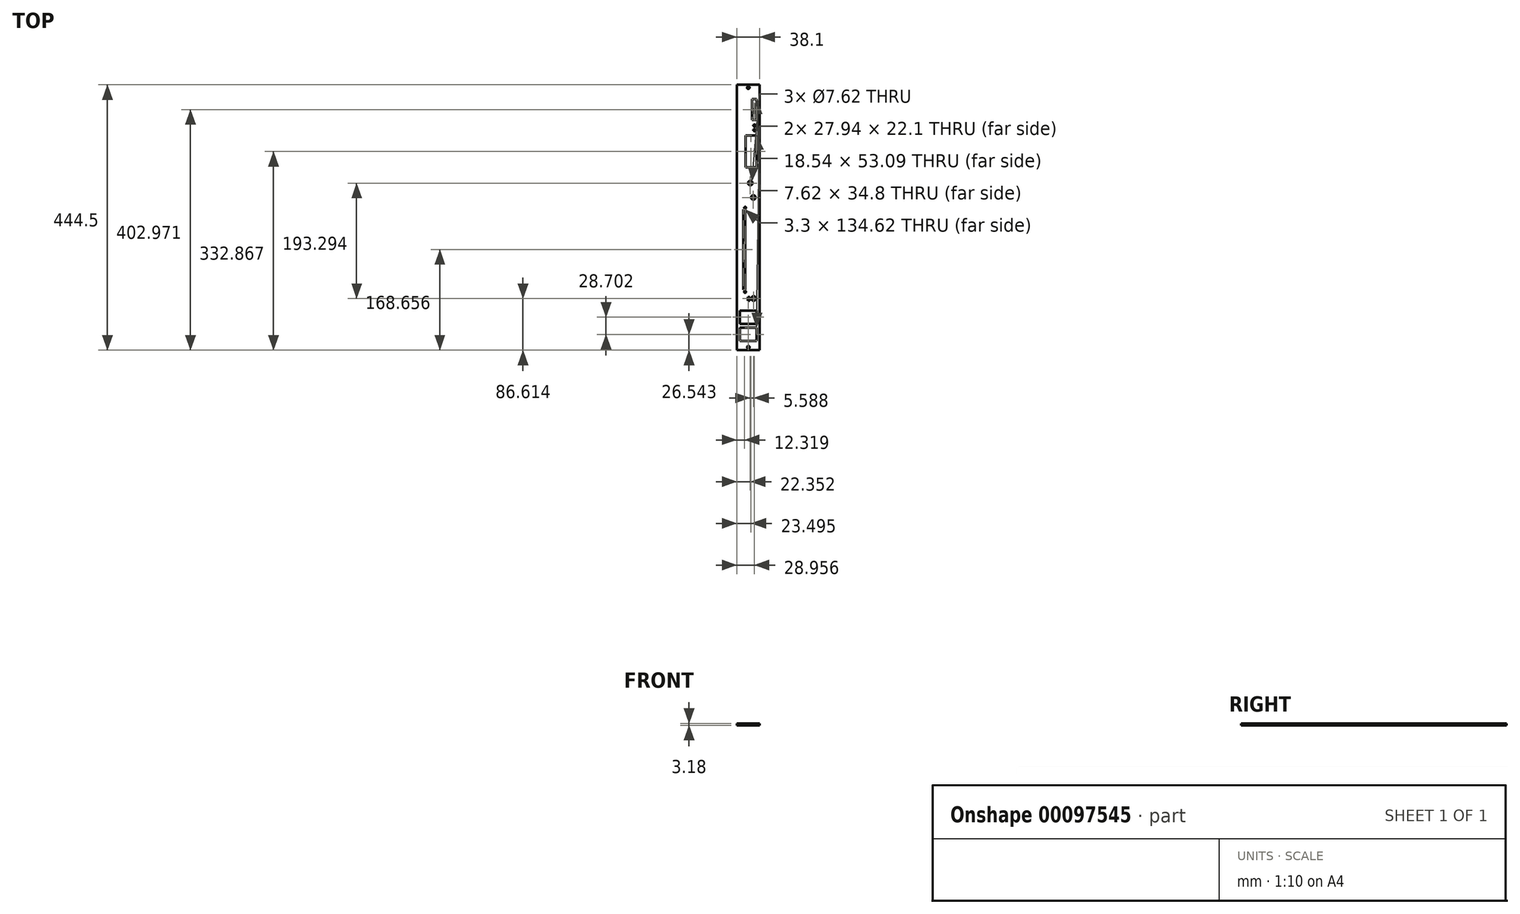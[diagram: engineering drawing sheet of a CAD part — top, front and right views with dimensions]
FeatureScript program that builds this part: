
annotation { "Feature Type Name" : "Feature", "Feature Type Description" : "" }
export const myFeature = defineFeature(function(context is Context, id is Id, definition is map)
    precondition{}
    {
        {
            var Q0;
            Q0=qCreatedBy(makeId("Top.planeOp"),FACE);
            var sketch = newSketch(context, id + "F0", { "sketchPlane" : qUnion([Q0])});
            skLineSegment(sketch, "E0.bottom", {"start": v(-19.05, 222.25) * mm, "end": v(19.05, 222.25) * mm});
            skLineSegment(sketch, "E0.top", {"start": v(-19.05, -222.25) * mm, "end": v(19.05, -222.25) * mm});
            skLineSegment(sketch, "E0.left", {"start": v(-19.05, 222.25) * mm, "end": v(-19.05, -222.25) * mm});
            skLineSegment(sketch, "E0.right", {"start": v(19.05, 222.25) * mm, "end": v(19.05, -222.25) * mm});
            skCircle(sketch, "E1", {"center": v(0, 217.55) * mm, "radius": 2.16 * mm});
            skLineSegment(sketch, "E2", {"start": v(0, 222.25) * mm, "end": v(0, -222.25) * mm, "construction": true});
            skCircle(sketch, "E3", {"center": v(0, -217.3) * mm, "radius": 2.16 * mm});
            skLineSegment(sketch, "E4.bottom", {"start": v(-13.97, -184.66) * mm, "end": v(13.97, -184.66) * mm});
            skLineSegment(sketch, "E4.top", {"start": v(-13.97, -206.76) * mm, "end": v(13.97, -206.76) * mm});
            skLineSegment(sketch, "E4.left", {"start": v(-13.97, -184.66) * mm, "end": v(-13.97, -206.76) * mm});
            skLineSegment(sketch, "E4.right", {"start": v(13.97, -184.66) * mm, "end": v(13.97, -206.76) * mm});
            skLineSegment(sketch, "E5.bottom", {"start": v(-13.97, -155.96) * mm, "end": v(13.97, -155.96) * mm});
            skLineSegment(sketch, "E5.top", {"start": v(-13.97, -178.05) * mm, "end": v(13.97, -178.05) * mm});
            skLineSegment(sketch, "E5.left", {"start": v(-13.97, -155.96) * mm, "end": v(-13.97, -178.05) * mm});
            skLineSegment(sketch, "E5.right", {"start": v(13.97, -155.96) * mm, "end": v(13.97, -178.05) * mm});
            skLineSegment(sketch, "E6.bottom", {"start": v(-8.38, 13.72) * mm, "end": v(-5.08, 13.72) * mm});
            skLineSegment(sketch, "E6.top", {"start": v(-8.38, -120.9) * mm, "end": v(-5.08, -120.9) * mm});
            skLineSegment(sketch, "E6.left", {"start": v(-8.38, 13.72) * mm, "end": v(-8.38, -120.9) * mm});
            skLineSegment(sketch, "E6.right", {"start": v(-5.08, 13.72) * mm, "end": v(-5.08, -120.9) * mm});
            skCircle(sketch, "E7", {"center": v(-5.33, -124.71) * mm, "radius": 1.52 * mm});
            skPoint(sketch, "E7.centerSnap0", {"position": v(-6.73, -120.9) * mm});
            skCircle(sketch, "E8", {"center": v(-5.33, 16.26) * mm, "radius": 1.52 * mm});
            skPoint(sketch, "E8.centerSnap0", {"position": v(-6.73, 13.72) * mm});
            skCircle(sketch, "E9", {"center": v(8.38, 33.53) * mm, "radius": 3.81 * mm});
            skCircle(sketch, "E10", {"center": v(3.3, 57.66) * mm, "radius": 3.81 * mm});
            skLineSegment(sketch, "E11.bottom", {"start": v(-4.83, 84.07) * mm, "end": v(13.72, 84.07) * mm});
            skLineSegment(sketch, "E11.top", {"start": v(-4.83, 137.16) * mm, "end": v(13.72, 137.16) * mm});
            skLineSegment(sketch, "E11.left", {"start": v(-4.83, 84.07) * mm, "end": v(-4.83, 137.16) * mm});
            skLineSegment(sketch, "E11.right", {"start": v(13.72, 84.07) * mm, "end": v(13.72, 137.16) * mm});
            skLineSegment(sketch, "E12.bottom", {"start": v(6.1, 198.12) * mm, "end": v(13.72, 198.12) * mm});
            skLineSegment(sketch, "E12.top", {"start": v(6.1, 163.32) * mm, "end": v(13.72, 163.32) * mm});
            skLineSegment(sketch, "E12.left", {"start": v(6.1, 198.12) * mm, "end": v(6.1, 163.32) * mm});
            skLineSegment(sketch, "E12.right", {"start": v(13.72, 198.12) * mm, "end": v(13.72, 163.32) * mm});
            skCircle(sketch, "E13", {"center": v(10.29, 154.05) * mm, "radius": 1.9 * mm});
            skCircle(sketch, "E14", {"center": v(10.29, 146.43) * mm, "radius": 1.9 * mm});
            skLineSegment(sketch, "E15.bottom", {"start": v(-1.02, -133.1) * mm, "end": v(2.54, -133.1) * mm});
            skLineSegment(sketch, "E15.top", {"start": v(-1.02, -139.2) * mm, "end": v(2.54, -139.2) * mm});
            skLineSegment(sketch, "E15.left", {"start": v(-1.02, -133.1) * mm, "end": v(-1.02, -139.2) * mm});
            skLineSegment(sketch, "E15.right", {"start": v(2.54, -133.1) * mm, "end": v(2.54, -139.2) * mm});
            skCircle(sketch, "E16", {"center": v(8.9, -135.64) * mm, "radius": 3.81 * mm});
            skSolve(sketch);
        }
        {
            var Q0;
            Q0=makeQuery(id+"F0.imprint","IMPRINT",FACE,{"disambiguationData":[TD([[makeQuery(id+"F0.imprint","IMPRINT",EDGE,{"derivedFrom":sQuery(id+"F0.wireOp",EDGE,"E0.bottom")}),-1.0]])]});
            extrude(context, id + "F1", {"entities" : qUnion([Q0]), "depth" : 3.17 * mm});
        }
    });
